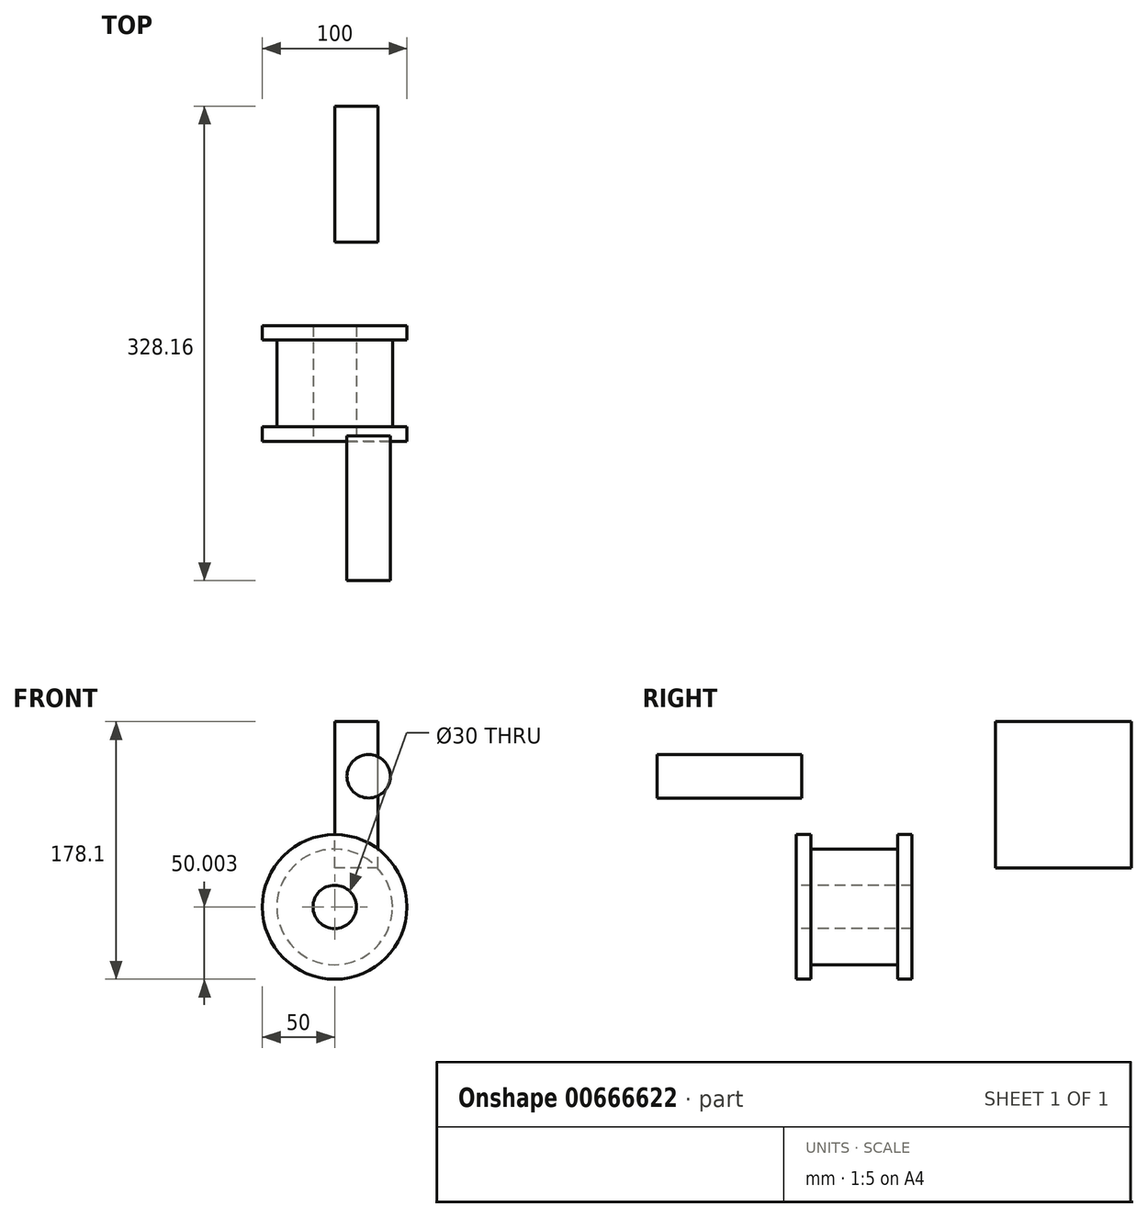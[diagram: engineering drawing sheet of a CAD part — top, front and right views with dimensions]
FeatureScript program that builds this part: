
annotation { "Feature Type Name" : "Feature", "Feature Type Description" : "" }
export const myFeature = defineFeature(function(context is Context, id is Id, definition is map)
    precondition{}
    {
        {
            var Q0;
            Q0=qCreatedBy(makeId("Front.planeOp"),FACE);
            var sketch = newSketch(context, id + "F0", { "sketchPlane" : qUnion([Q0])});
            skCircle(sketch, "E0", {"center": v(23.5, 10.43) * mm, "radius": 15 * mm});
            skSolve(sketch);
        }
        {
            var Q0;
            Q0=makeQuery(id+"F0.imprint","IMPRINT",FACE,{"disambiguationData":[TD([[makeQuery(id+"F0.imprint","IMPRINT",EDGE,{"derivedFrom":sQuery(id+"F0.wireOp",EDGE,"E0")}),1.0]])]});
            extrude(context, id + "F1", {"entities" : qUnion([Q0]), "depth" : 100 * mm, "offsetDistance" : 25 * mm});
        }
        {
            var Q0;
            Q0=qCreatedBy(makeId("Right.planeOp"),FACE);
            var sketch = newSketch(context, id + "F2", { "sketchPlane" : qUnion([Q0])});
            skLineSegment(sketch, "E1", {"start": v(-3.66, -79.9) * mm, "end": v(-3.66, -29.9) * mm});
            skLineSegment(sketch, "E2", {"start": v(-3.66, -29.9) * mm, "end": v(6.34, -29.9) * mm});
            skLineSegment(sketch, "E3", {"start": v(6.34, -29.9) * mm, "end": v(6.34, -39.9) * mm});
            skLineSegment(sketch, "E4", {"start": v(6.34, -39.9) * mm, "end": v(66.34, -39.9) * mm});
            skLineSegment(sketch, "E5", {"start": v(66.34, -39.9) * mm, "end": v(66.34, -29.9) * mm});
            skLineSegment(sketch, "E6", {"start": v(66.34, -29.9) * mm, "end": v(76.34, -29.9) * mm});
            skLineSegment(sketch, "E7", {"start": v(76.34, -29.9) * mm, "end": v(76.34, -79.9) * mm});
            skLineSegment(sketch, "E8", {"start": v(76.34, -79.9) * mm, "end": v(-3.66, -79.9) * mm});
            skSolve(sketch);
        }
        {
            var Q0;
            Q0=makeQuery(id+"F2.imprint","IMPRINT",FACE,{"disambiguationData":[TD([[makeQuery(id+"F2.imprint","IMPRINT",EDGE,{"derivedFrom":sQuery(id+"F2.wireOp",EDGE,"E1")}),-1.0]])]});
            var Q1;
            Q1=sQuery(id+"F2.wireOp",EDGE,"E8");
            revolve(context, id + "F3", {"surfaceOperationType" : NewSurfaceOperationType.NEW, "entities" : qUnion([Q0]), "axis" : qUnion([Q1]), "revolveType" : RevolveType.FULL});
        }
        {
            var Q0;
            Q0=makeQuery(id+"F3.opRevolve","SWEPT_FACE",FACE,{"disambiguationData":[OSD([sQuery(id+"F2.wireOp",EDGE,"E1")])]});
            var sketch = newSketch(context, id + "F4", { "sketchPlane" : qUnion([Q0])});
            skCircle(sketch, "E9", {"center": v(0, -79.9) * mm, "radius": 15 * mm});
            skSolve(sketch);
        }
        {
            var Q0;
            Q0=makeQuery(id+"F4.imprint","IMPRINT",FACE,{"disambiguationData":[TD([[makeQuery(id+"F4.imprint","IMPRINT",EDGE,{"derivedFrom":sQuery(id+"F4.wireOp",EDGE,"E9")}),1.0]])]});
            extrude(context, id + "F5", {"entities" : qUnion([Q0]), "operationType" : NewBodyOperationType.REMOVE, "oppositeDirection" : true, "depth" : 80 * mm, "offsetDistance" : 25 * mm});
        }
        {
            var Q0;
            Q0=qCreatedBy(makeId("Right.planeOp"),FACE);
            var sketch = newSketch(context, id + "F6", { "sketchPlane" : qUnion([Q0])});
            skLineSegment(sketch, "E10.bottom", {"start": v(228.16, -52.8) * mm, "end": v(134.16, -52.8) * mm});
            skLineSegment(sketch, "E10.top", {"start": v(228.16, 48.2) * mm, "end": v(134.16, 48.2) * mm});
            skLineSegment(sketch, "E10.left", {"start": v(228.16, -52.8) * mm, "end": v(228.16, 48.2) * mm});
            skLineSegment(sketch, "E10.right", {"start": v(134.16, -52.8) * mm, "end": v(134.16, 48.2) * mm});
            skPoint(sketch, "E10.middle", {"position": v(181.16, -2.3) * mm});
            skSolve(sketch);
        }
        {
            var Q0;
            Q0=makeQuery(id+"F6.imprint","IMPRINT",FACE,{"disambiguationData":[TD([[makeQuery(id+"F6.imprint","IMPRINT",EDGE,{"derivedFrom":sQuery(id+"F6.wireOp",EDGE,"E10.bottom")}),-1.0]])]});
            extrude(context, id + "F7", {"entities" : qUnion([Q0]), "depth" : 30 * mm, "offsetDistance" : 25 * mm});
        }
    });
